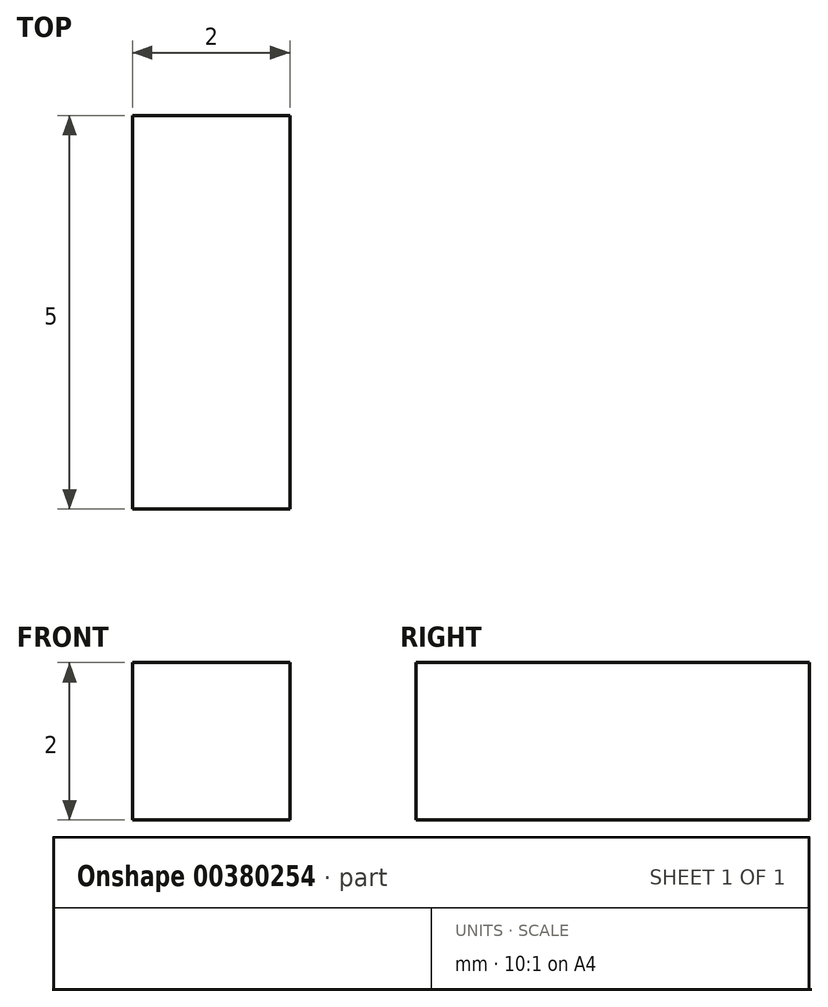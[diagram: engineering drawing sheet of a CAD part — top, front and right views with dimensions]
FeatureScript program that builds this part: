
annotation { "Feature Type Name" : "Feature", "Feature Type Description" : "" }
export const myFeature = defineFeature(function(context is Context, id is Id, definition is map)
    precondition{}
    {
        {
            var Q0;
            Q0=qCreatedBy(makeId("Top.planeOp"),FACE);
            var sketch = newSketch(context, id + "F0", { "sketchPlane" : qUnion([Q0])});
            skLineSegment(sketch, "E0.bottom", {"start": v(25, -25) * mm, "end": v(-25, -25) * mm});
            skLineSegment(sketch, "E0.top", {"start": v(25, 25) * mm, "end": v(-25, 25) * mm});
            skLineSegment(sketch, "E0.left", {"start": v(25, -25) * mm, "end": v(25, 25) * mm});
            skLineSegment(sketch, "E0.right", {"start": v(-25, -25) * mm, "end": v(-25, 25) * mm});
            skPoint(sketch, "E0.middle", {"position": v(0, 0) * mm});
            skLineSegment(sketch, "E1", {"start": v(-23, 28.59) * mm, "end": v(-23, -29.68) * mm, "construction": true});
            skLineSegment(sketch, "E2", {"start": v(23, 28.1) * mm, "end": v(23, -32.62) * mm, "construction": true});
            skLineSegment(sketch, "E3", {"start": v(-28.75, 20) * mm, "end": v(28.04, 20) * mm, "construction": true});
            skLineSegment(sketch, "E4", {"start": v(-28.75, -20) * mm, "end": v(32.46, -20) * mm, "construction": true});
            skLineSegment(sketch, "E5.bottom", {"start": v(-23, 25) * mm, "end": v(-25, 25) * mm});
            skLineSegment(sketch, "E5.top", {"start": v(-23, 20) * mm, "end": v(-25, 20) * mm});
            skLineSegment(sketch, "E5.left", {"start": v(-23, 25) * mm, "end": v(-23, 20) * mm});
            skLineSegment(sketch, "E5.right", {"start": v(-25, 25) * mm, "end": v(-25, 20) * mm});
            skLineSegment(sketch, "E6", {"start": v(-28.75, 15) * mm, "end": v(28.18, 15) * mm, "construction": true});
            skLineSegment(sketch, "E7", {"start": v(-28.75, 10) * mm, "end": v(28.18, 10) * mm, "construction": true});
            skLineSegment(sketch, "E8.bottom", {"start": v(-25, 15) * mm, "end": v(-23, 15) * mm, "construction": true});
            skLineSegment(sketch, "E8.top", {"start": v(-25, 10) * mm, "end": v(-23, 10) * mm, "construction": true});
            skLineSegment(sketch, "E8.left", {"start": v(-25, 15) * mm, "end": v(-25, 10) * mm, "construction": true});
            skLineSegment(sketch, "E8.right", {"start": v(-23, 15) * mm, "end": v(-23, 10) * mm, "construction": true});
            skLineSegment(sketch, "E9", {"start": v(-28.75, 5) * mm, "end": v(28.18, 5) * mm, "construction": true});
            skLineSegment(sketch, "E10", {"start": v(-28.75, 0) * mm, "end": v(28.18, 0) * mm, "construction": true});
            skLineSegment(sketch, "E11.bottom", {"start": v(-25, 5) * mm, "end": v(-23, 5) * mm});
            skLineSegment(sketch, "E11.top", {"start": v(-25, 0) * mm, "end": v(-23, 0) * mm});
            skLineSegment(sketch, "E11.left", {"start": v(-25, 5) * mm, "end": v(-25, 0) * mm});
            skLineSegment(sketch, "E11.right", {"start": v(-23, 5) * mm, "end": v(-23, 0) * mm});
            skLineSegment(sketch, "E12.bottom", {"start": v(-25, 15) * mm, "end": v(-23, 15) * mm});
            skLineSegment(sketch, "E12.top", {"start": v(-25, 10) * mm, "end": v(-23, 10) * mm});
            skLineSegment(sketch, "E12.left", {"start": v(-25, 15) * mm, "end": v(-25, 10) * mm});
            skLineSegment(sketch, "E12.right", {"start": v(-23, 15) * mm, "end": v(-23, 10) * mm});
            skLineSegment(sketch, "E13", {"start": v(-28.75, 0) * mm, "end": v(-28.75, -5) * mm, "construction": true});
            skLineSegment(sketch, "E14", {"start": v(-28.75, -5) * mm, "end": v(28.18, -5) * mm, "construction": true});
            skLineSegment(sketch, "E15", {"start": v(-28.75, -10) * mm, "end": v(28.18, -10) * mm, "construction": true});
            skLineSegment(sketch, "E16.bottom", {"start": v(-25, -5) * mm, "end": v(-23, -5) * mm});
            skLineSegment(sketch, "E16.top", {"start": v(-25, -10) * mm, "end": v(-23, -10) * mm});
            skLineSegment(sketch, "E16.left", {"start": v(-25, -5) * mm, "end": v(-25, -10) * mm});
            skLineSegment(sketch, "E16.right", {"start": v(-23, -5) * mm, "end": v(-23, -10) * mm});
            skLineSegment(sketch, "E17", {"start": v(-28.75, -15) * mm, "end": v(28.18, -15) * mm, "construction": true});
            skLineSegment(sketch, "E18.bottom", {"start": v(-25, -15) * mm, "end": v(-23, -15) * mm});
            skLineSegment(sketch, "E18.top", {"start": v(-25, -20) * mm, "end": v(-23, -20) * mm});
            skLineSegment(sketch, "E18.left", {"start": v(-25, -15) * mm, "end": v(-25, -20) * mm});
            skLineSegment(sketch, "E18.right", {"start": v(-23, -15) * mm, "end": v(-23, -20) * mm});
            skLineSegment(sketch, "E19.bottom", {"start": v(23, 20) * mm, "end": v(25, 20) * mm});
            skLineSegment(sketch, "E19.top", {"start": v(23, 15) * mm, "end": v(25, 15) * mm});
            skLineSegment(sketch, "E19.left", {"start": v(23, 20) * mm, "end": v(23, 15) * mm});
            skLineSegment(sketch, "E19.right", {"start": v(25, 20) * mm, "end": v(25, 15) * mm});
            skLineSegment(sketch, "E20.bottom", {"start": v(23, 10) * mm, "end": v(25, 10) * mm});
            skLineSegment(sketch, "E20.top", {"start": v(23, 5) * mm, "end": v(25, 5) * mm});
            skLineSegment(sketch, "E20.left", {"start": v(23, 10) * mm, "end": v(23, 5) * mm});
            skLineSegment(sketch, "E20.right", {"start": v(25, 10) * mm, "end": v(25, 5) * mm});
            skLineSegment(sketch, "E21.bottom", {"start": v(23, 0) * mm, "end": v(25, 0) * mm});
            skLineSegment(sketch, "E21.top", {"start": v(23, -5) * mm, "end": v(25, -5) * mm});
            skLineSegment(sketch, "E21.left", {"start": v(23, 0) * mm, "end": v(23, -5) * mm});
            skLineSegment(sketch, "E21.right", {"start": v(25, 0) * mm, "end": v(25, -5) * mm});
            skLineSegment(sketch, "E22.bottom", {"start": v(23, -10) * mm, "end": v(25, -10) * mm});
            skLineSegment(sketch, "E22.top", {"start": v(23, -15) * mm, "end": v(25, -15) * mm});
            skLineSegment(sketch, "E22.left", {"start": v(23, -10) * mm, "end": v(23, -15) * mm});
            skLineSegment(sketch, "E22.right", {"start": v(25, -10) * mm, "end": v(25, -15) * mm});
            skLineSegment(sketch, "E23.bottom", {"start": v(23, -20) * mm, "end": v(25, -20) * mm});
            skLineSegment(sketch, "E23.top", {"start": v(23, -25) * mm, "end": v(25, -25) * mm});
            skLineSegment(sketch, "E23.left", {"start": v(23, -20) * mm, "end": v(23, -25) * mm});
            skLineSegment(sketch, "E23.right", {"start": v(25, -20) * mm, "end": v(25, -25) * mm});
            skSolve(sketch);
        }
        {
            var Q0;
            {var subQ18=sQuery(id+"F0.wireOp",EDGE,"E0.bottom");Q0=makeQuery(id+"F0.imprint","IMPRINT",FACE,{"disambiguationData":[TD([[makeQuery(id+"F0.imprint","IMPRINT",EDGE,{"derivedFrom":subQ18}),-1.0]])]});}
            extrude(context, id + "F1", {"entities" : qUnion([Q0]), "depth" : 2 * mm});
        }
    });
